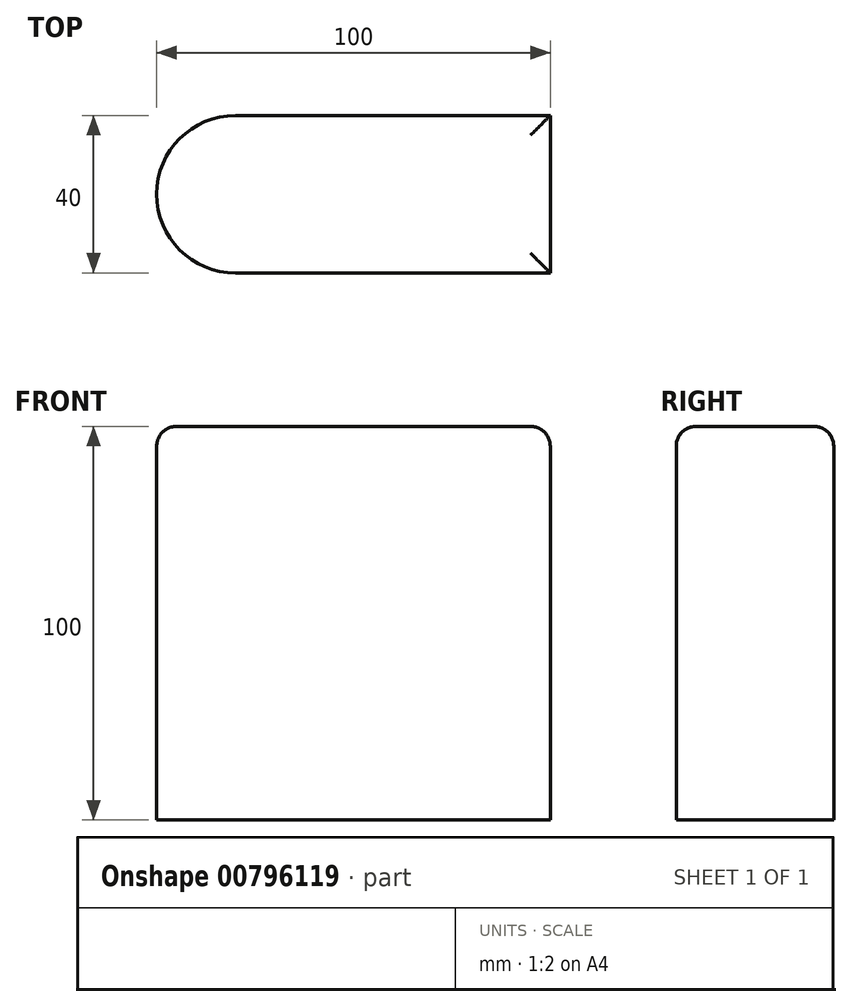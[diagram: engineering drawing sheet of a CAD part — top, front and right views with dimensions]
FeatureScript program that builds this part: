
annotation { "Feature Type Name" : "Feature", "Feature Type Description" : "" }
export const myFeature = defineFeature(function(context is Context, id is Id, definition is map)
    precondition{}
    {
        {
            var Q0;
            Q0=qCreatedBy(makeId("Top.planeOp"),FACE);
            var sketch = newSketch(context, id + "F0", { "sketchPlane" : qUnion([Q0])});
            skLineSegment(sketch, "E0.bottom", {"start": v(-40, 20) * mm, "end": v(40, 20) * mm});
            skLineSegment(sketch, "E0.top", {"start": v(-40, -20) * mm, "end": v(40, -20) * mm});
            skLineSegment(sketch, "E0.left", {"start": v(-40, 20) * mm, "end": v(-40, -20) * mm, "construction": true});
            skLineSegment(sketch, "E0.right", {"start": v(40, 20) * mm, "end": v(40, -20) * mm});
            skArc(sketch, "E1", {"start": v(-40, 20) * mm, "mid": v(-60, 0) * mm, "end": v(-40, -20) * mm});
            skSolve(sketch);
        }
        {
            var Q0;
            Q0 = qSketchRegion(id + "F0", true);
            extrude(context, id + "F1", {"entities" : qUnion([Q0]), "depth" : 100 * mm, "offsetDistance" : 25 * mm});
        }
        {
            var Q0;
            Q0=makeQuery(id+"F1.opExtrude","CAP_EDGE",EDGE,{"disambiguationData":[OSD([sQuery(id+"F0.wireOp",EDGE,"E0.bottom")])],"isStart":false});
            var Q1;
            Q1=makeQuery(id+"F1.opExtrude","CAP_EDGE",EDGE,{"disambiguationData":[OSD([sQuery(id+"F0.wireOp",EDGE,"E0.right")])],"isStart":false});
            fillet(context, id + "F2", {"entities" : qUnion([Q0, Q1]), "radius" : 5 * mm, "tangentPropagation" : true, "allowEdgeOverflow" : false});
        }
    });
